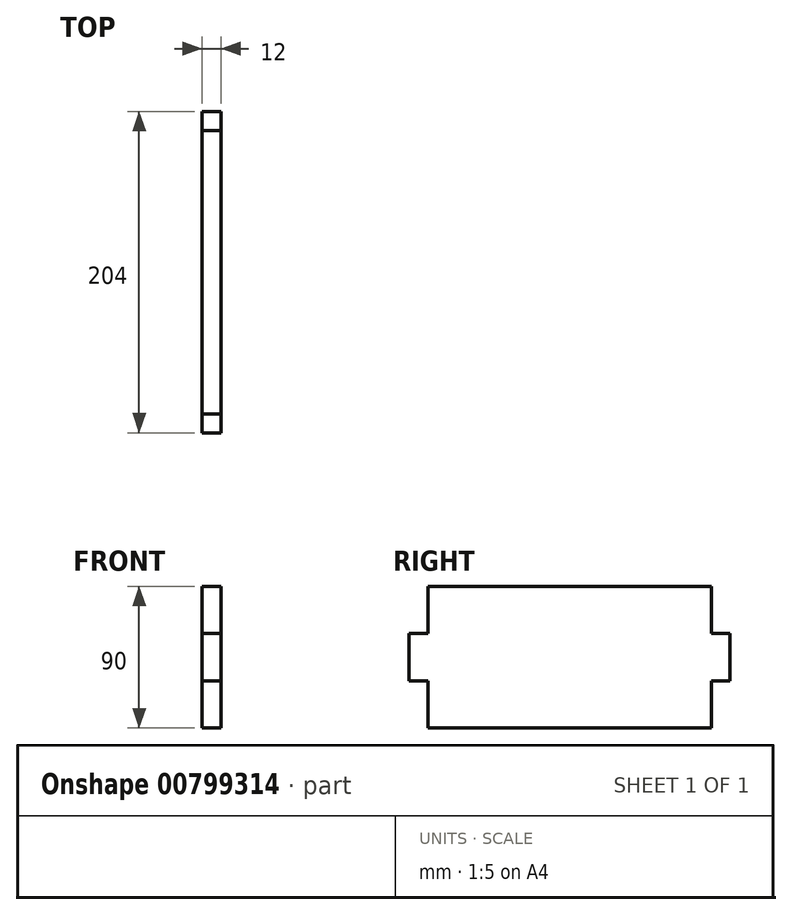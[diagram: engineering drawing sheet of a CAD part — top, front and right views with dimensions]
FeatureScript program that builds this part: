
annotation { "Feature Type Name" : "Feature", "Feature Type Description" : "" }
export const myFeature = defineFeature(function(context is Context, id is Id, definition is map)
    precondition{}
    {
        {
            var Q0;
            Q0=qCreatedBy(makeId("Right.planeOp"),FACE);
            var sketch = newSketch(context, id + "F0", { "sketchPlane" : qUnion([Q0])});
            skLineSegment(sketch, "E0", {"start": v(0, 0) * mm, "end": v(0, 30) * mm});
            skLineSegment(sketch, "E1", {"start": v(-12, 30) * mm, "end": v(0, 30) * mm});
            skLineSegment(sketch, "E2", {"start": v(-12, 30) * mm, "end": v(-12, 60) * mm});
            skLineSegment(sketch, "E3", {"start": v(-12, 60) * mm, "end": v(0, 60) * mm});
            skLineSegment(sketch, "E4", {"start": v(0, 90) * mm, "end": v(0, 60) * mm});
            skLineSegment(sketch, "E5", {"start": v(0, 90) * mm, "end": v(180, 90) * mm});
            skLineSegment(sketch, "E6", {"start": v(180, 90) * mm, "end": v(180, 60) * mm});
            skLineSegment(sketch, "E7", {"start": v(180, 60) * mm, "end": v(192, 60) * mm});
            skLineSegment(sketch, "E8", {"start": v(192, 60) * mm, "end": v(192, 30) * mm});
            skLineSegment(sketch, "E9", {"start": v(192, 30) * mm, "end": v(180, 30) * mm});
            skLineSegment(sketch, "E10", {"start": v(180, 0) * mm, "end": v(180, 30) * mm});
            skLineSegment(sketch, "E11", {"start": v(180, 0) * mm, "end": v(0, 0) * mm});
            skSolve(sketch);
        }
        {
            var Q0;
            Q0 = qSketchRegion(id + "F0", true);
            extrude(context, id + "F1", {"entities" : qUnion([Q0]), "depth" : 12 * mm, "offsetDistance" : 25.4 * mm});
        }
    });
